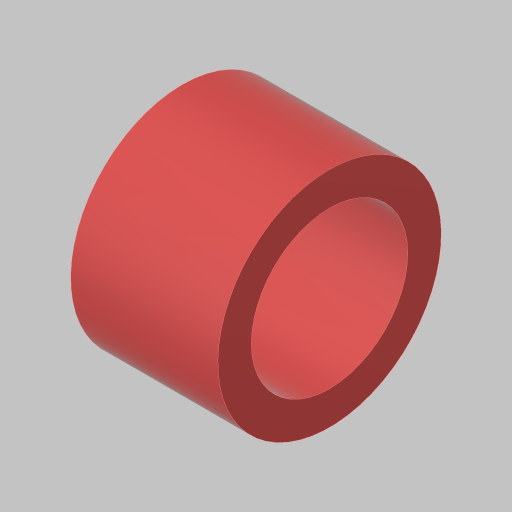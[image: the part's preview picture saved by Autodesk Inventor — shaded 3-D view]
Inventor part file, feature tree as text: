
AUTODESK INVENTOR PART (.ipt)
format: ipt  version: 2023.5 (Build 275446000, 446)  size: 114,688 bytes
history: native  units: in
note: dims shown in document units (in); Inventor stores cm internally (conversion verified against a paired STEP export)
features: extrude x1, sketch x1
ambient origin geometry x8: Origin, YZ Plane, XZ Plane, XY Plane, X Axis, Y Axis, Z Axis, Center Point
bodies: Solid1 (feature_tree)
feature tree (2):
  extrude  "Extrusion1"  Depth=0.55in
  sketch  "Sketch1"  dims[d0=0.585in d1=0.125in d2=0.55in d3=0.0in]
